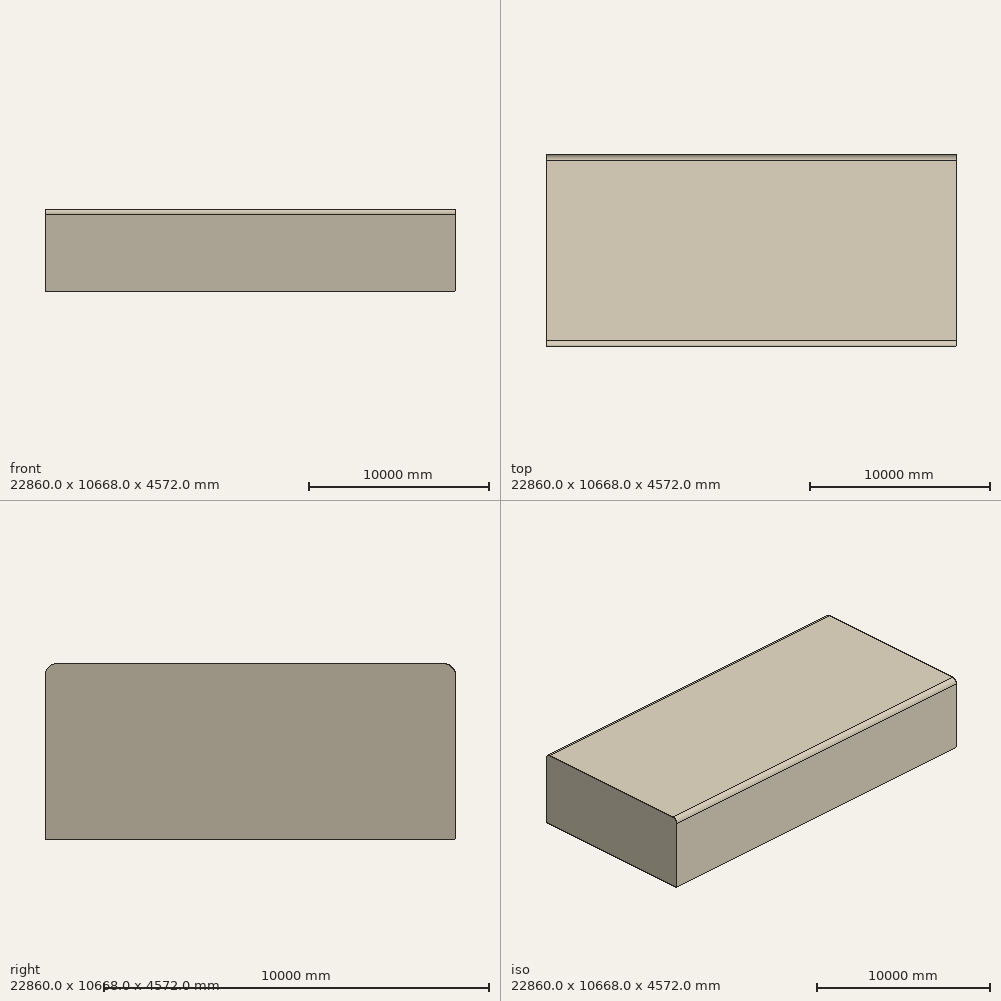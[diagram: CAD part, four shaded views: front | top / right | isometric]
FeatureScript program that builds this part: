
annotation { "Feature Type Name" : "Feature", "Feature Type Description" : "" }
export const myFeature = defineFeature(function(context is Context, id is Id, definition is map)
    precondition{}
    {
        {
            var Q0;
            Q0=qCreatedBy(makeId("Top.planeOp"),FACE);
            var sketch = newSketch(context, id + "F1", { "sketchPlane" : qUnion([Q0])});
            skLineSegment(sketch, "E0.bottom", {"start": v(0, 0) * mm, "end": v(-22860, 0) * mm});
            skLineSegment(sketch, "E0.top", {"start": v(0, 10668) * mm, "end": v(-22860, 10668) * mm});
            skLineSegment(sketch, "E0.left", {"start": v(0, 0) * mm, "end": v(0, 10668) * mm});
            skLineSegment(sketch, "E0.right", {"start": v(-22860, 0) * mm, "end": v(-22860, 10668) * mm});
            skSolve(sketch);
        }
        {
            var Q0;
            Q0 = qSketchRegion(id + "F1", true);
            extrude(context, id + "F2", {"entities" : qUnion([Q0]), "depth" : 4572 * mm});
        }
        {
            var Q0;
            Q0=makeQuery(id+"F2.opExtrude","CAP_EDGE",EDGE,{"disambiguationData":[OSD([sQuery(id+"F1.wireOp",EDGE,"E0.bottom")])],"isStart":false});
            var Q1;
            Q1=makeQuery(id+"F2.opExtrude","CAP_EDGE",EDGE,{"disambiguationData":[OSD([sQuery(id+"F1.wireOp",EDGE,"E0.top")])],"isStart":false});
            fillet(context, id + "F0", {"entities" : qUnion([Q0, Q1]), "radius" : 304.8 * mm, "tangentPropagation" : true, "allowEdgeOverflow" : false});
        }
    });
